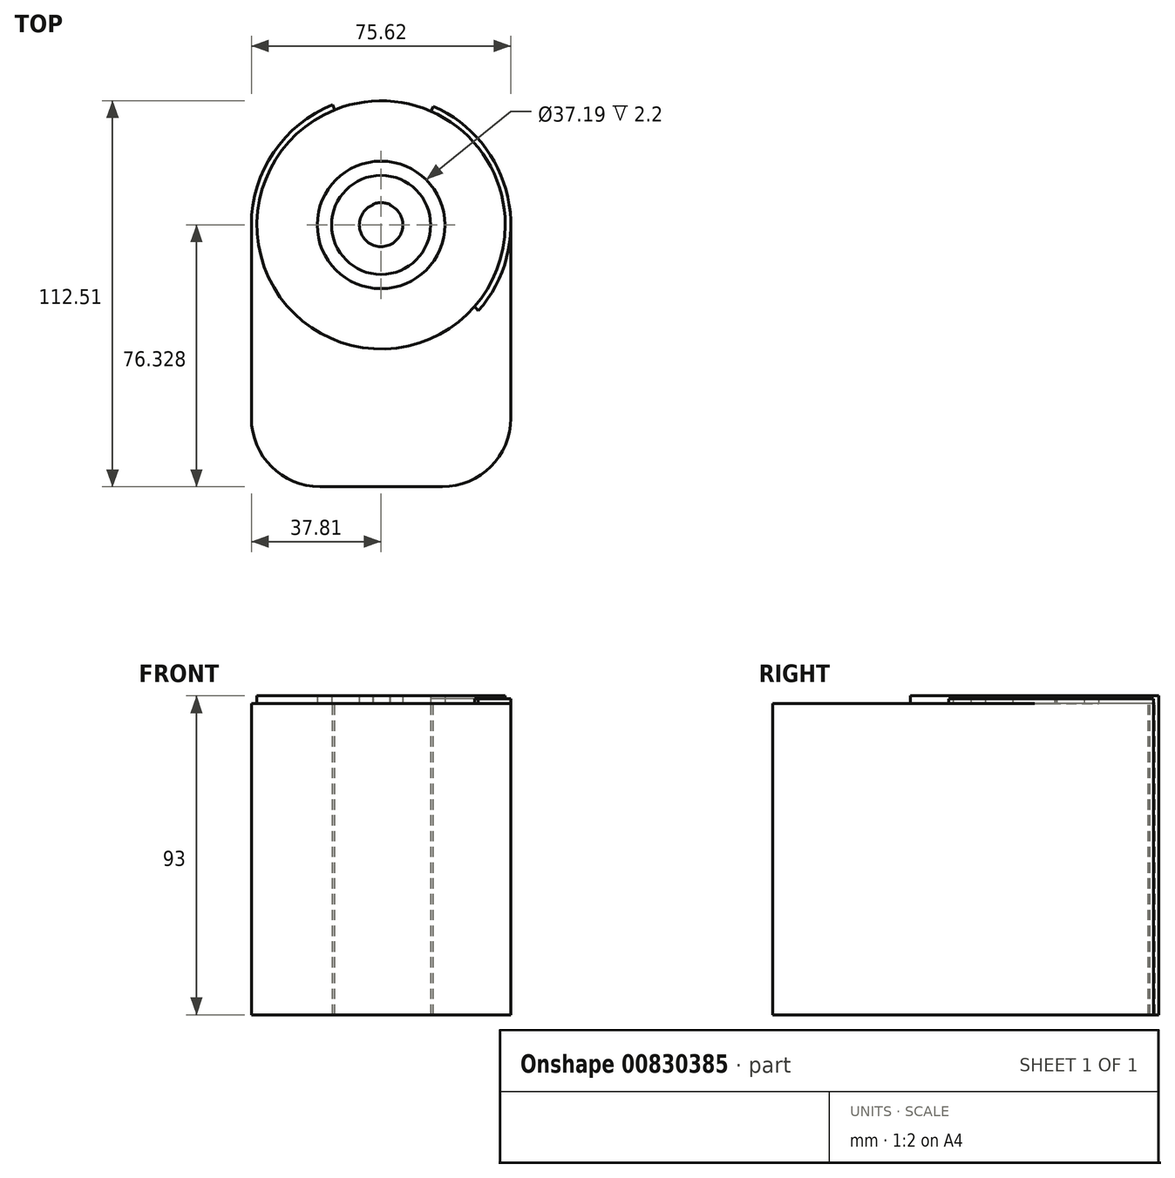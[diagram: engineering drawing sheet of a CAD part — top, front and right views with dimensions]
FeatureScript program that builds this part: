
annotation { "Feature Type Name" : "Feature", "Feature Type Description" : "" }
export const myFeature = defineFeature(function(context is Context, id is Id, definition is map)
    precondition{}
    {
        {
            var Q0;
            Q0=qCreatedBy(makeId("Top.planeOp"),FACE);
            var sketch = newSketch(context, id + "F0", { "sketchPlane" : qUnion([Q0])});
            skPoint(sketch, "E0", {"position": v(0, 0) * mm});
            skCircle(sketch, "E1", {"center": v(0, 37.75) * mm, "radius": 37.8 * mm});
            skLineSegment(sketch, "E2.top", {"start": v(-17.8, -38.58) * mm, "end": v(17.8, -38.58) * mm});
            skLineSegment(sketch, "E2.left", {"start": v(-37.8, 37.75) * mm, "end": v(-37.8, -18.58) * mm});
            skLineSegment(sketch, "E2.right", {"start": v(37.8, 37.75) * mm, "end": v(37.8, -18.58) * mm});
            skCircle(sketch, "E3", {"center": v(0, 37.75) * mm, "radius": 36.18 * mm});
            skPoint(sketch, "E4", {"position": v(-74.9, 75.54) * mm});
            skPoint(sketch, "E5", {"position": v(74.77, 75.16) * mm});
            skLineSegment(sketch, "E6", {"start": v(-74.9, 75.54) * mm, "end": v(74.77, 75.16) * mm});
            skPoint(sketch, "E7", {"position": v(0, 75.26) * mm});
            skPoint(sketch, "E8", {"position": v(-26.77, 64.44) * mm});
            skPoint(sketch, "E9", {"position": v(26.84, 64.38) * mm});
            skPoint(sketch, "E10.visualSharp", {"position": v(-37.8, -38.58) * mm});
            skArc(sketch, "E10.filletArc", {"start": v(-37.8, -18.58) * mm, "mid": v(-31.95, -32.72) * mm, "end": v(-17.8, -38.58) * mm});
            skPoint(sketch, "E11.visualSharp", {"position": v(37.8, -38.58) * mm});
            skArc(sketch, "E11.filletArc", {"start": v(17.8, -38.58) * mm, "mid": v(31.95, -32.72) * mm, "end": v(37.8, -18.58) * mm});
            skPoint(sketch, "E12", {"position": v(0, -38.58) * mm});
            skPoint(sketch, "E13", {"position": v(37.8, 9.58) * mm});
            skPoint(sketch, "E14", {"position": v(-37.8, 9.58) * mm});
            skCircle(sketch, "E15", {"center": v(0, 37.75) * mm, "radius": 14.44 * mm});
            skCircle(sketch, "E16", {"center": v(0, 37.75) * mm, "radius": 6.33 * mm});
            skPoint(sketch, "E17", {"position": v(-14.08, 72.84) * mm});
            skPoint(sketch, "E18", {"position": v(15.23, 72.35) * mm});
            skLineSegment(sketch, "E19", {"start": v(-14.08, 72.84) * mm, "end": v(0, 37.75) * mm});
            skLineSegment(sketch, "E20", {"start": v(15.23, 72.35) * mm, "end": v(0, 37.75) * mm});
            skCircle(sketch, "E21", {"center": v(0, 37.75) * mm, "radius": 18.6 * mm});
            skPoint(sketch, "E22", {"position": v(0, 9.58) * mm});
            skLineSegment(sketch, "E23.top", {"start": v(-11.25, -32.72) * mm, "end": v(11.95, -32.72) * mm});
            skLineSegment(sketch, "E23.left", {"start": v(-31.25, 3.58) * mm, "end": v(-31.25, -12.72) * mm});
            skLineSegment(sketch, "E23.right", {"start": v(31.95, 3.58) * mm, "end": v(31.95, -12.72) * mm});
            skPoint(sketch, "E24.visualSharp", {"position": v(-31.25, -32.72) * mm});
            skArc(sketch, "E24.filletArc", {"start": v(-31.25, -12.72) * mm, "mid": v(-25.4, -26.86) * mm, "end": v(-11.25, -32.72) * mm});
            skPoint(sketch, "E25.visualSharp", {"position": v(31.95, -32.72) * mm});
            skArc(sketch, "E25.filletArc", {"start": v(11.95, -32.72) * mm, "mid": v(26.1, -26.86) * mm, "end": v(31.95, -12.72) * mm});
            skPoint(sketch, "E26", {"position": v(-22.72, 9.58) * mm});
            skPoint(sketch, "E27", {"position": v(22.72, 9.58) * mm});
            skPoint(sketch, "E28", {"position": v(-25.22, 9.58) * mm});
            skPoint(sketch, "E29", {"position": v(25.22, 9.58) * mm});
            skLineSegment(sketch, "E30", {"start": v(-25.25, 9.58) * mm, "end": v(-25.22, 9.58) * mm});
            skLineSegment(sketch, "E31", {"start": v(25.95, 9.58) * mm, "end": v(25.22, 9.58) * mm});
            skPoint(sketch, "E32", {"position": v(-2.36, 43.62) * mm});
            skPoint(sketch, "E33", {"position": v(2.55, 43.54) * mm});
            skPoint(sketch, "E34", {"position": v(5.82, 50.96) * mm});
            skPoint(sketch, "E35", {"position": v(-5.38, 51.15) * mm});
            skPoint(sketch, "E36", {"position": v(-6.93, 55) * mm});
            skPoint(sketch, "E37", {"position": v(7.5, 54.77) * mm});
            skPoint(sketch, "E38.visualSharp", {"position": v(-31.25, 9.58) * mm});
            skArc(sketch, "E38.filletArc", {"start": v(-25.25, 9.58) * mm, "mid": v(-29.5, 7.83) * mm, "end": v(-31.25, 3.58) * mm});
            skPoint(sketch, "E39.visualSharp", {"position": v(31.95, 9.58) * mm});
            skArc(sketch, "E39.filletArc", {"start": v(31.95, 3.58) * mm, "mid": v(30.2, 7.83) * mm, "end": v(25.95, 9.58) * mm});
            skLineSegment(sketch, "E40", {"start": v(0, 37.75) * mm, "end": v(42.74, -15.84) * mm});
            skArc(sketch, "E41.0.startCap", {"start": v(-5.08, 33.7) * mm, "mid": v(-4.05, 42.83) * mm, "end": v(5.08, 41.8) * mm});
            skArc(sketch, "E41.0.endCap", {"start": v(47.83, -11.79) * mm, "mid": v(46.8, -20.92) * mm, "end": v(37.66, -19.9) * mm});
            skLineSegment(sketch, "E41.0.left", {"start": v(5.08, 41.8) * mm, "end": v(47.83, -11.79) * mm});
            skLineSegment(sketch, "E41.0.right", {"start": v(-5.08, 33.7) * mm, "end": v(37.66, -19.9) * mm});
            skCircle(sketch, "E42", {"center": v(42.74, -15.84) * mm, "radius": 8.34 * mm});
            skLineSegment(sketch, "E43", {"start": v(37.8, 37.75) * mm, "end": v(37.8, -27.66) * mm});
            skSolve(sketch);
        }
        {
            var Q0;
            {var subQ1=sQuery(id+"F0.wireOp",EDGE,"E1");var subQ7=sQuery(id+"F0.wireOp",EDGE,"E20");var subQ10=makeQuery(id+"F0.imprint","INTERSECT",VERTEX,{"derivedFrom":[subQ1,subQ7]});Q0=makeQuery(id+"F0.imprint","IMPRINT",FACE,{"disambiguationData":[TD([[makeQuery(id+"F0.imprint","IMPRINT",EDGE,{"disambiguationData":[TD([[subQ10,-1.0]])],"derivedFrom":subQ1}),1.0]])]});}
            var Q1;
            {var subQ0=sQuery(id+"F0.wireOp",EDGE,"E1");var subQ6=makeQuery(id+"F0.imprint","INTERSECT",VERTEX,{"derivedFrom":[subQ0,sQuery(id+"F0.wireOp",EDGE,"E2.left")]});Q1=makeQuery(id+"F0.imprint","IMPRINT",FACE,{"disambiguationData":[TD([[makeQuery(id+"F0.imprint","IMPRINT",EDGE,{"disambiguationData":[TD([[subQ6,1.0]])],"derivedFrom":subQ0}),1.0]])]});}
            var Q2;
            {var subQ0=sQuery(id+"F0.wireOp",EDGE,"E20");var subQ1=sQuery(id+"F0.wireOp",EDGE,"E1");var subQ2=makeQuery(id+"F0.imprint","INTERSECT",VERTEX,{"derivedFrom":[subQ1,subQ0]});Q2=makeQuery(id+"F0.imprint","IMPRINT",FACE,{"disambiguationData":[TD([[makeQuery(id+"F0.imprint","IMPRINT",EDGE,{"disambiguationData":[TD([[subQ2,1.0]])],"derivedFrom":subQ1}),1.0]])]});}
            var Q3;
            {var subQ0=sQuery(id+"F0.wireOp",EDGE,"E19");var subQ1=sQuery(id+"F0.wireOp",EDGE,"E3");var subQ2=makeQuery(id+"F0.imprint","INTERSECT",VERTEX,{"derivedFrom":[subQ1,subQ0]});Q3=makeQuery(id+"F0.imprint","IMPRINT",FACE,{"disambiguationData":[TD([[makeQuery(id+"F0.imprint","IMPRINT",EDGE,{"disambiguationData":[TD([[subQ2,1.0]])],"derivedFrom":subQ1}),1.0]])]});}
            var Q4;
            {var subQ0=sQuery(id+"F0.wireOp",EDGE,"E20");var subQ1=sQuery(id+"F0.wireOp",EDGE,"E3");var subQ2=makeQuery(id+"F0.imprint","INTERSECT",VERTEX,{"derivedFrom":[subQ1,subQ0]});Q4=makeQuery(id+"F0.imprint","IMPRINT",FACE,{"disambiguationData":[TD([[makeQuery(id+"F0.imprint","IMPRINT",EDGE,{"disambiguationData":[TD([[subQ2,1.0]])],"derivedFrom":subQ1}),1.0]])]});}
            var Q5;
            {var subQ0=sQuery(id+"F0.wireOp",EDGE,"E19");var subQ1=sQuery(id+"F0.wireOp",EDGE,"E3");var subQ2=makeQuery(id+"F0.imprint","INTERSECT",VERTEX,{"derivedFrom":[subQ1,subQ0]});Q5=makeQuery(id+"F0.imprint","IMPRINT",FACE,{"disambiguationData":[TD([[makeQuery(id+"F0.imprint","IMPRINT",EDGE,{"disambiguationData":[TD([[subQ2,-1.0]])],"derivedFrom":subQ1}),1.0]])]});}
            var Q6;
            {var subQ0=sQuery(id+"F0.wireOp",EDGE,"E19");var subQ1=sQuery(id+"F0.wireOp",EDGE,"E15");var subQ2=makeQuery(id+"F0.imprint","INTERSECT",VERTEX,{"derivedFrom":[subQ1,subQ0]});Q6=makeQuery(id+"F0.imprint","IMPRINT",FACE,{"disambiguationData":[TD([[makeQuery(id+"F0.imprint","IMPRINT",EDGE,{"disambiguationData":[TD([[subQ2,1.0]])],"derivedFrom":subQ1}),-1.0]])]});}
            var Q7;
            {var subQ0=sQuery(id+"F0.wireOp",EDGE,"E19");var subQ1=sQuery(id+"F0.wireOp",EDGE,"E15");var subQ2=makeQuery(id+"F0.imprint","INTERSECT",VERTEX,{"derivedFrom":[subQ1,subQ0]});Q7=makeQuery(id+"F0.imprint","IMPRINT",FACE,{"disambiguationData":[TD([[makeQuery(id+"F0.imprint","IMPRINT",EDGE,{"disambiguationData":[TD([[subQ2,-1.0]])],"derivedFrom":subQ1}),-1.0]])]});}
            var Q8;
            {var subQ0=sQuery(id+"F0.wireOp",EDGE,"E20");var subQ1=sQuery(id+"F0.wireOp",EDGE,"E15");var subQ2=makeQuery(id+"F0.imprint","INTERSECT",VERTEX,{"derivedFrom":[subQ1,subQ0]});Q8=makeQuery(id+"F0.imprint","IMPRINT",FACE,{"disambiguationData":[TD([[makeQuery(id+"F0.imprint","IMPRINT",EDGE,{"disambiguationData":[TD([[subQ2,1.0]])],"derivedFrom":subQ1}),-1.0]])]});}
            var Q9;
            {var subQ0=sQuery(id+"F0.wireOp",EDGE,"E40");var subQ1=sQuery(id+"F0.wireOp",EDGE,"E15");var subQ2=makeQuery(id+"F0.imprint","INTERSECT",VERTEX,{"derivedFrom":[subQ1,subQ0]});Q9=makeQuery(id+"F0.imprint","IMPRINT",FACE,{"disambiguationData":[TD([[makeQuery(id+"F0.imprint","IMPRINT",EDGE,{"disambiguationData":[TD([[subQ2,-1.0]])],"derivedFrom":subQ1}),1.0]])]});}
            var Q10;
            {var subQ5=sQuery(id+"F0.wireOp",EDGE,"E15");var subQ9=sQuery(id+"F0.wireOp",EDGE,"E41.0.right");var subQ10=makeQuery(id+"F0.imprint","INTERSECT",VERTEX,{"derivedFrom":[subQ5,subQ9]});Q10=makeQuery(id+"F0.imprint","IMPRINT",FACE,{"disambiguationData":[TD([[makeQuery(id+"F0.imprint","IMPRINT",EDGE,{"disambiguationData":[TD([[subQ10,-1.0]])],"derivedFrom":subQ5}),1.0]])]});}
            var Q11;
            {var subQ0=sQuery(id+"F0.wireOp",EDGE,"E19");var subQ1=sQuery(id+"F0.wireOp",EDGE,"E16");var subQ2=makeQuery(id+"F0.imprint","INTERSECT",VERTEX,{"derivedFrom":[subQ1,subQ0]});Q11=makeQuery(id+"F0.imprint","IMPRINT",FACE,{"disambiguationData":[TD([[makeQuery(id+"F0.imprint","IMPRINT",EDGE,{"disambiguationData":[TD([[subQ2,1.0]])],"derivedFrom":subQ1}),-1.0]])]});}
            var Q12;
            {var subQ0=sQuery(id+"F0.wireOp",EDGE,"E19");var subQ1=sQuery(id+"F0.wireOp",EDGE,"E15");var subQ2=makeQuery(id+"F0.imprint","INTERSECT",VERTEX,{"derivedFrom":[subQ1,subQ0]});Q12=makeQuery(id+"F0.imprint","IMPRINT",FACE,{"disambiguationData":[TD([[makeQuery(id+"F0.imprint","IMPRINT",EDGE,{"disambiguationData":[TD([[subQ2,1.0]])],"derivedFrom":subQ1}),1.0]])]});}
            var Q13;
            {var subQ0=sQuery(id+"F0.wireOp",EDGE,"E19");var subQ1=sQuery(id+"F0.wireOp",EDGE,"E16");var subQ2=makeQuery(id+"F0.imprint","INTERSECT",VERTEX,{"derivedFrom":[subQ1,subQ0]});Q13=makeQuery(id+"F0.imprint","IMPRINT",FACE,{"disambiguationData":[TD([[makeQuery(id+"F0.imprint","IMPRINT",EDGE,{"disambiguationData":[TD([[subQ2,1.0]])],"derivedFrom":subQ1}),1.0]])]});}
            var Q14;
            {var subQ0=sQuery(id+"F0.wireOp",EDGE,"E20");var subQ1=sQuery(id+"F0.wireOp",EDGE,"E16");var subQ2=makeQuery(id+"F0.imprint","INTERSECT",VERTEX,{"derivedFrom":[subQ1,subQ0]});Q14=makeQuery(id+"F0.imprint","IMPRINT",FACE,{"disambiguationData":[TD([[makeQuery(id+"F0.imprint","IMPRINT",EDGE,{"disambiguationData":[TD([[subQ2,1.0]])],"derivedFrom":subQ1}),1.0]])]});}
            var Q15;
            {var subQ0=sQuery(id+"F0.wireOp",EDGE,"E19");var subQ1=sQuery(id+"F0.wireOp",EDGE,"E16");var subQ2=makeQuery(id+"F0.imprint","INTERSECT",VERTEX,{"derivedFrom":[subQ1,subQ0]});Q15=makeQuery(id+"F0.imprint","IMPRINT",FACE,{"disambiguationData":[TD([[makeQuery(id+"F0.imprint","IMPRINT",EDGE,{"disambiguationData":[TD([[subQ2,-1.0]])],"derivedFrom":subQ1}),1.0]])]});}
            var Q16;
            {var subQ0=sQuery(id+"F0.wireOp",EDGE,"E20");var subQ1=sQuery(id+"F0.wireOp",EDGE,"E15");var subQ2=makeQuery(id+"F0.imprint","INTERSECT",VERTEX,{"derivedFrom":[subQ1,subQ0]});Q16=makeQuery(id+"F0.imprint","IMPRINT",FACE,{"disambiguationData":[TD([[makeQuery(id+"F0.imprint","IMPRINT",EDGE,{"disambiguationData":[TD([[subQ2,1.0]])],"derivedFrom":subQ1}),1.0]])]});}
            var Q17;
            {var subQ0=sQuery(id+"F0.wireOp",EDGE,"E19");var subQ1=sQuery(id+"F0.wireOp",EDGE,"E15");var subQ2=makeQuery(id+"F0.imprint","INTERSECT",VERTEX,{"derivedFrom":[subQ1,subQ0]});Q17=makeQuery(id+"F0.imprint","IMPRINT",FACE,{"disambiguationData":[TD([[makeQuery(id+"F0.imprint","IMPRINT",EDGE,{"disambiguationData":[TD([[subQ2,-1.0]])],"derivedFrom":subQ1}),1.0]])]});}
            var Q18;
            {var subQ0=sQuery(id+"F0.wireOp",EDGE,"E40");var subQ1=sQuery(id+"F0.wireOp",EDGE,"E15");var subQ2=makeQuery(id+"F0.imprint","INTERSECT",VERTEX,{"derivedFrom":[subQ1,subQ0]});Q18=makeQuery(id+"F0.imprint","IMPRINT",FACE,{"disambiguationData":[TD([[makeQuery(id+"F0.imprint","IMPRINT",EDGE,{"disambiguationData":[TD([[subQ2,-1.0]])],"derivedFrom":subQ1}),-1.0]])]});}
            var Q19;
            {var subQ0=sQuery(id+"F0.wireOp",EDGE,"E40");var subQ1=sQuery(id+"F0.wireOp",EDGE,"E3");var subQ2=makeQuery(id+"F0.imprint","INTERSECT",VERTEX,{"derivedFrom":[subQ1,subQ0]});Q19=makeQuery(id+"F0.imprint","IMPRINT",FACE,{"disambiguationData":[TD([[makeQuery(id+"F0.imprint","IMPRINT",EDGE,{"disambiguationData":[TD([[subQ2,-1.0]])],"derivedFrom":subQ1}),1.0]])]});}
            var Q20;
            {var subQ0=sQuery(id+"F0.wireOp",EDGE,"E41.0.right");var subQ1=sQuery(id+"F0.wireOp",EDGE,"E3");var subQ2=makeQuery(id+"F0.imprint","INTERSECT",VERTEX,{"derivedFrom":[subQ1,subQ0]});Q20=makeQuery(id+"F0.imprint","IMPRINT",FACE,{"disambiguationData":[TD([[makeQuery(id+"F0.imprint","IMPRINT",EDGE,{"disambiguationData":[TD([[subQ2,-1.0]])],"derivedFrom":subQ1}),1.0]])]});}
            var Q21;
            {var subQ0=sQuery(id+"F0.wireOp",EDGE,"E41.0.right");var subQ1=sQuery(id+"F0.wireOp",EDGE,"E15");var subQ2=makeQuery(id+"F0.imprint","INTERSECT",VERTEX,{"derivedFrom":[subQ1,subQ0]});Q21=makeQuery(id+"F0.imprint","IMPRINT",FACE,{"disambiguationData":[TD([[makeQuery(id+"F0.imprint","IMPRINT",EDGE,{"disambiguationData":[TD([[subQ2,-1.0]])],"derivedFrom":subQ1}),-1.0]])]});}
            var Q22;
            {var subQ5=sQuery(id+"F0.wireOp",EDGE,"E1");var subQ6=makeQuery(id+"F0.imprint","INTERSECT",VERTEX,{"derivedFrom":[subQ5,sQuery(id+"F0.wireOp",EDGE,"E31")]});Q22=makeQuery(id+"F0.imprint","IMPRINT",FACE,{"disambiguationData":[TD([[makeQuery(id+"F0.imprint","IMPRINT",EDGE,{"disambiguationData":[TD([[subQ6,1.0]])],"derivedFrom":subQ5}),1.0]])]});}
            var Q23;
            {var subQ0=sQuery(id+"F0.wireOp",EDGE,"E41.0.right");var subQ1=sQuery(id+"F0.wireOp",EDGE,"E1");var subQ2=makeQuery(id+"F0.imprint","INTERSECT",VERTEX,{"derivedFrom":[subQ1,subQ0]});Q23=makeQuery(id+"F0.imprint","IMPRINT",FACE,{"disambiguationData":[TD([[makeQuery(id+"F0.imprint","IMPRINT",EDGE,{"disambiguationData":[TD([[subQ2,-1.0]])],"derivedFrom":subQ1}),1.0]])]});}
            var Q24;
            {var subQ0=sQuery(id+"F0.wireOp",EDGE,"E31");Q24=makeQuery(id+"F0.imprint","IMPRINT",FACE,{"disambiguationData":[TD([[makeQuery(id+"F0.imprint","IMPRINT",EDGE,{"derivedFrom":subQ0}),1.0]])]});}
            var Q25;
            {var subQ1=sQuery(id+"F0.wireOp",EDGE,"E31");Q25=makeQuery(id+"F0.imprint","IMPRINT",FACE,{"disambiguationData":[TD([[makeQuery(id+"F0.imprint","IMPRINT",EDGE,{"derivedFrom":subQ1}),-1.0]])]});}
            var Q26;
            {var subQ1=sQuery(id+"F0.wireOp",EDGE,"E1");var subQ7=sQuery(id+"F0.wireOp",EDGE,"E41.0.right");var subQ9=makeQuery(id+"F0.imprint","INTERSECT",VERTEX,{"derivedFrom":[subQ1,subQ7]});Q26=makeQuery(id+"F0.imprint","IMPRINT",FACE,{"disambiguationData":[TD([[makeQuery(id+"F0.imprint","IMPRINT",EDGE,{"disambiguationData":[TD([[subQ9,-1.0]])],"derivedFrom":subQ1}),-1.0]])]});}
            var Q27;
            {var subQ1=sQuery(id+"F0.wireOp",EDGE,"E25.filletArc");var subQ6=sQuery(id+"F0.wireOp",EDGE,"E23.right");var subQ9=makeQuery(id+"F0.imprint","INTERSECT",VERTEX,{"derivedFrom":[subQ6,subQ1]});Q27=makeQuery(id+"F0.imprint","IMPRINT",FACE,{"disambiguationData":[TD([[makeQuery(id+"F0.imprint","IMPRINT",EDGE,{"disambiguationData":[TD([[subQ9,1.0]])],"derivedFrom":subQ6}),1.0]])]});}
            var Q28;
            {var subQ5=sQuery(id+"F0.wireOp",EDGE,"E43");var subQ9=sQuery(id+"F0.wireOp",EDGE,"E11.filletArc");var subQ10=makeQuery(id+"F0.imprint","INTERSECT",VERTEX,{"derivedFrom":[subQ9,subQ5]});Q28=makeQuery(id+"F0.imprint","IMPRINT",FACE,{"disambiguationData":[TD([[makeQuery(id+"F0.imprint","IMPRINT",EDGE,{"disambiguationData":[TD([[subQ10,1.0]])],"derivedFrom":subQ9}),1.0]])]});}
            var Q29;
            {var subQ0=sQuery(id+"F0.wireOp",EDGE,"E43");var subQ1=sQuery(id+"F0.wireOp",EDGE,"E40");var subQ2=makeQuery(id+"F0.imprint","INTERSECT",VERTEX,{"derivedFrom":[subQ1,subQ0]});Q29=makeQuery(id+"F0.imprint","IMPRINT",FACE,{"disambiguationData":[TD([[makeQuery(id+"F0.imprint","IMPRINT",EDGE,{"disambiguationData":[TD([[subQ2,1.0]])],"derivedFrom":subQ1}),1.0]])]});}
            var Q30;
            {var subQ0=sQuery(id+"F0.wireOp",EDGE,"E42");var subQ1=sQuery(id+"F0.wireOp",EDGE,"E11.filletArc");var subQ2=makeQuery(id+"F0.imprint","INTERSECT",VERTEX,{"derivedFrom":[subQ1,subQ0]});Q30=makeQuery(id+"F0.imprint","IMPRINT",FACE,{"disambiguationData":[TD([[makeQuery(id+"F0.imprint","IMPRINT",EDGE,{"disambiguationData":[TD([[subQ2,-1.0]])],"derivedFrom":subQ1}),1.0]])]});}
            var Q31;
            {var subQ5=sQuery(id+"F0.wireOp",EDGE,"E2.top");Q31=makeQuery(id+"F0.imprint","IMPRINT",FACE,{"disambiguationData":[TD([[makeQuery(id+"F0.imprint","IMPRINT",EDGE,{"derivedFrom":subQ5}),1.0]])]});}
            var Q32;
            {var subQ0=sQuery(id+"F0.wireOp",EDGE,"E23.top");Q32=makeQuery(id+"F0.imprint","IMPRINT",FACE,{"disambiguationData":[TD([[makeQuery(id+"F0.imprint","IMPRINT",EDGE,{"derivedFrom":subQ0}),1.0]])]});}
            var Q33;
            {var subQ0=sQuery(id+"F0.wireOp",EDGE,"E43");var subQ1=sQuery(id+"F0.wireOp",EDGE,"E1");var subQ2=makeQuery(id+"F0.imprint","INTERSECT",VERTEX,{"derivedFrom":[subQ1,subQ0]});Q33=makeQuery(id+"F0.imprint","IMPRINT",FACE,{"disambiguationData":[TD([[makeQuery(id+"F0.imprint","IMPRINT",EDGE,{"disambiguationData":[TD([[subQ2,1.0]])],"derivedFrom":subQ1}),-1.0]])]});}
            extrude(context, id + "F1", {"entities" : qUnion([Q0, Q1, Q2, Q3, Q4, Q5, Q6, Q7, Q8, Q9, Q10, Q11, Q12, Q13, Q14, Q15, Q16, Q17, Q18, Q19, Q20, Q21, Q22, Q23, Q24, Q25, Q26, Q27, Q28, Q29, Q30, Q31, Q32, Q33]), "oppositeDirection" : true, "depth" : 90.8 * mm, "offsetDistance" : 25 * mm});
        }
        {
            var Q0;
            {var subQ0=sQuery(id+"F0.wireOp",EDGE,"E20");var subQ1=sQuery(id+"F0.wireOp",EDGE,"E3");var subQ2=makeQuery(id+"F0.imprint","INTERSECT",VERTEX,{"derivedFrom":[subQ1,subQ0]});Q0=makeQuery(id+"F0.imprint","IMPRINT",FACE,{"disambiguationData":[TD([[makeQuery(id+"F0.imprint","IMPRINT",EDGE,{"disambiguationData":[TD([[subQ2,1.0]])],"derivedFrom":subQ1}),1.0]])]});}
            var Q1;
            {var subQ0=sQuery(id+"F0.wireOp",EDGE,"E40");var subQ1=sQuery(id+"F0.wireOp",EDGE,"E3");var subQ2=makeQuery(id+"F0.imprint","INTERSECT",VERTEX,{"derivedFrom":[subQ1,subQ0]});Q1=makeQuery(id+"F0.imprint","IMPRINT",FACE,{"disambiguationData":[TD([[makeQuery(id+"F0.imprint","IMPRINT",EDGE,{"disambiguationData":[TD([[subQ2,-1.0]])],"derivedFrom":subQ1}),1.0]])]});}
            var Q2;
            {var subQ0=sQuery(id+"F0.wireOp",EDGE,"E41.0.right");var subQ1=sQuery(id+"F0.wireOp",EDGE,"E3");var subQ2=makeQuery(id+"F0.imprint","INTERSECT",VERTEX,{"derivedFrom":[subQ1,subQ0]});Q2=makeQuery(id+"F0.imprint","IMPRINT",FACE,{"disambiguationData":[TD([[makeQuery(id+"F0.imprint","IMPRINT",EDGE,{"disambiguationData":[TD([[subQ2,-1.0]])],"derivedFrom":subQ1}),1.0]])]});}
            var Q3;
            {var subQ0=sQuery(id+"F0.wireOp",EDGE,"E19");var subQ1=sQuery(id+"F0.wireOp",EDGE,"E3");var subQ2=makeQuery(id+"F0.imprint","INTERSECT",VERTEX,{"derivedFrom":[subQ1,subQ0]});Q3=makeQuery(id+"F0.imprint","IMPRINT",FACE,{"disambiguationData":[TD([[makeQuery(id+"F0.imprint","IMPRINT",EDGE,{"disambiguationData":[TD([[subQ2,-1.0]])],"derivedFrom":subQ1}),1.0]])]});}
            var Q4;
            {var subQ0=sQuery(id+"F0.wireOp",EDGE,"E19");var subQ1=sQuery(id+"F0.wireOp",EDGE,"E3");var subQ2=makeQuery(id+"F0.imprint","INTERSECT",VERTEX,{"derivedFrom":[subQ1,subQ0]});Q4=makeQuery(id+"F0.imprint","IMPRINT",FACE,{"disambiguationData":[TD([[makeQuery(id+"F0.imprint","IMPRINT",EDGE,{"disambiguationData":[TD([[subQ2,1.0]])],"derivedFrom":subQ1}),1.0]])]});}
            var Q5;
            {var subQ0=sQuery(id+"F0.wireOp",EDGE,"E20");var subQ1=sQuery(id+"F0.wireOp",EDGE,"E15");var subQ2=makeQuery(id+"F0.imprint","INTERSECT",VERTEX,{"derivedFrom":[subQ1,subQ0]});Q5=makeQuery(id+"F0.imprint","IMPRINT",FACE,{"disambiguationData":[TD([[makeQuery(id+"F0.imprint","IMPRINT",EDGE,{"disambiguationData":[TD([[subQ2,1.0]])],"derivedFrom":subQ1}),1.0]])]});}
            var Q6;
            {var subQ0=sQuery(id+"F0.wireOp",EDGE,"E40");var subQ1=sQuery(id+"F0.wireOp",EDGE,"E15");var subQ2=makeQuery(id+"F0.imprint","INTERSECT",VERTEX,{"derivedFrom":[subQ1,subQ0]});Q6=makeQuery(id+"F0.imprint","IMPRINT",FACE,{"disambiguationData":[TD([[makeQuery(id+"F0.imprint","IMPRINT",EDGE,{"disambiguationData":[TD([[subQ2,-1.0]])],"derivedFrom":subQ1}),1.0]])]});}
            var Q7;
            {var subQ5=sQuery(id+"F0.wireOp",EDGE,"E15");var subQ9=sQuery(id+"F0.wireOp",EDGE,"E41.0.right");var subQ10=makeQuery(id+"F0.imprint","INTERSECT",VERTEX,{"derivedFrom":[subQ5,subQ9]});Q7=makeQuery(id+"F0.imprint","IMPRINT",FACE,{"disambiguationData":[TD([[makeQuery(id+"F0.imprint","IMPRINT",EDGE,{"disambiguationData":[TD([[subQ10,-1.0]])],"derivedFrom":subQ5}),1.0]])]});}
            var Q8;
            {var subQ0=sQuery(id+"F0.wireOp",EDGE,"E19");var subQ1=sQuery(id+"F0.wireOp",EDGE,"E15");var subQ2=makeQuery(id+"F0.imprint","INTERSECT",VERTEX,{"derivedFrom":[subQ1,subQ0]});Q8=makeQuery(id+"F0.imprint","IMPRINT",FACE,{"disambiguationData":[TD([[makeQuery(id+"F0.imprint","IMPRINT",EDGE,{"disambiguationData":[TD([[subQ2,-1.0]])],"derivedFrom":subQ1}),1.0]])]});}
            var Q9;
            {var subQ0=sQuery(id+"F0.wireOp",EDGE,"E19");var subQ1=sQuery(id+"F0.wireOp",EDGE,"E15");var subQ2=makeQuery(id+"F0.imprint","INTERSECT",VERTEX,{"derivedFrom":[subQ1,subQ0]});Q9=makeQuery(id+"F0.imprint","IMPRINT",FACE,{"disambiguationData":[TD([[makeQuery(id+"F0.imprint","IMPRINT",EDGE,{"disambiguationData":[TD([[subQ2,1.0]])],"derivedFrom":subQ1}),1.0]])]});}
            extrude(context, id + "F2", {"entities" : qUnion([Q0, Q1, Q2, Q3, Q4, Q5, Q6, Q7, Q8, Q9]), "operationType" : NewBodyOperationType.ADD, "depth" : 2.2 * mm, "offsetDistance" : 25 * mm});
        }
        {
            var Q0;
            {var subQ1=sQuery(id+"F0.wireOp",EDGE,"E1");var subQ7=sQuery(id+"F0.wireOp",EDGE,"E20");var subQ10=makeQuery(id+"F0.imprint","INTERSECT",VERTEX,{"derivedFrom":[subQ1,subQ7]});Q0=makeQuery(id+"F0.imprint","IMPRINT",FACE,{"disambiguationData":[TD([[makeQuery(id+"F0.imprint","IMPRINT",EDGE,{"disambiguationData":[TD([[subQ10,-1.0]])],"derivedFrom":subQ1}),1.0]])]});}
            extrude(context, id + "F3", {"entities" : qUnion([Q0]), "operationType" : NewBodyOperationType.REMOVE, "oppositeDirection" : true, "depth" : 98.2 * mm, "offsetDistance" : 25 * mm});
        }
        {
            var Q0;
            {var subQ0=sQuery(id+"F0.wireOp",EDGE,"E20");var subQ1=sQuery(id+"F0.wireOp",EDGE,"E1");var subQ2=makeQuery(id+"F0.imprint","INTERSECT",VERTEX,{"derivedFrom":[subQ1,subQ0]});Q0=makeQuery(id+"F0.imprint","IMPRINT",FACE,{"disambiguationData":[TD([[makeQuery(id+"F0.imprint","IMPRINT",EDGE,{"disambiguationData":[TD([[subQ2,1.0]])],"derivedFrom":subQ1}),1.0]])]});}
            extrude(context, id + "F4", {"entities" : qUnion([Q0]), "operationType" : NewBodyOperationType.ADD, "depth" : 1.3 * mm, "offsetDistance" : 25 * mm});
        }
    });
